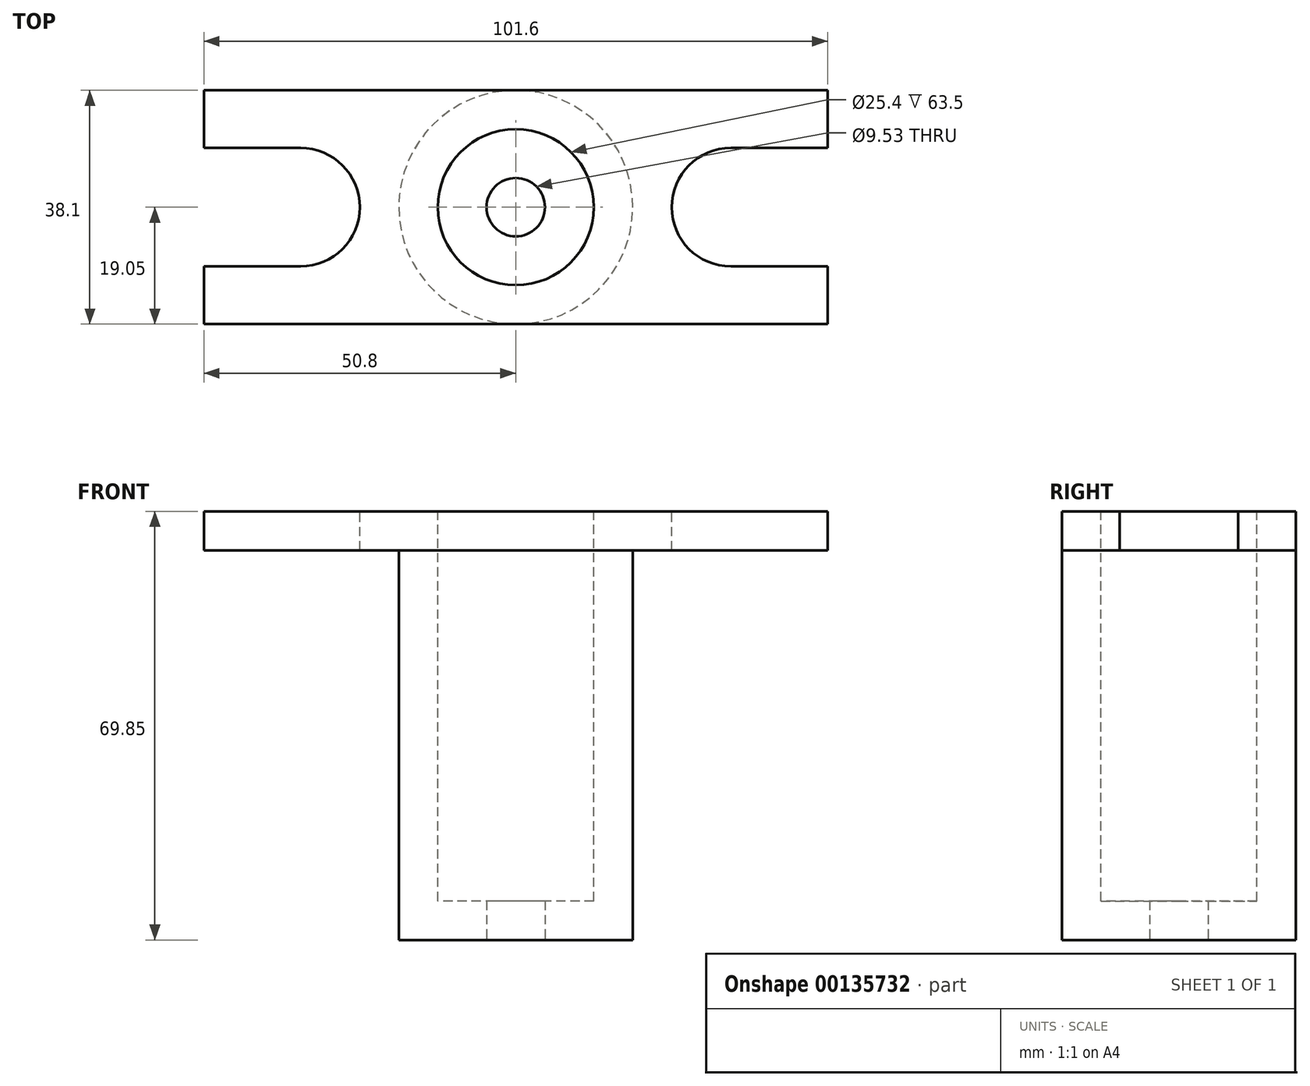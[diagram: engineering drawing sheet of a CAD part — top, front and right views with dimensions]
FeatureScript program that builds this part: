
annotation { "Feature Type Name" : "Feature", "Feature Type Description" : "" }
export const myFeature = defineFeature(function(context is Context, id is Id, definition is map)
    precondition{}
    {
        {
            var Q0;
            Q0=qCreatedBy(makeId("Top.planeOp"),FACE);
            var sketch = newSketch(context, id + "F0", { "sketchPlane" : qUnion([Q0])});
            skCircle(sketch, "E0", {"center": v(0, 0) * mm, "radius": 19.05 * mm});
            skSolve(sketch);
        }
        {
            var Q0;
            Q0 = qSketchRegion(id + "F0", true);
            extrude(context, id + "F1", {"entities" : qUnion([Q0]), "depth" : 69.85 * mm});
        }
        {
            var Q0;
            Q0=makeQuery(id+"F1.opExtrude","CAP_FACE",FACE,{"disambiguationData":[OSD([sQuery(id+"F0.wireOp",EDGE,"E0")])],"isStart":false});
            var sketch = newSketch(context, id + "F2", { "sketchPlane" : qUnion([Q0])});
            skCircle(sketch, "E1", {"center": v(0, 0) * mm, "radius": 12.7 * mm});
            skSolve(sketch);
        }
        {
            var Q0;
            Q0 = qSketchRegion(id + "F2", true);
            extrude(context, id + "F3", {"entities" : qUnion([Q0]), "operationType" : NewBodyOperationType.REMOVE, "oppositeDirection" : true, "depth" : 63.5 * mm});
        }
        {
            var Q0;
            Q0=makeQuery(id+"F1.opExtrude","CAP_FACE",FACE,{"disambiguationData":[OSD([sQuery(id+"F0.wireOp",EDGE,"E0")])],"isStart":false});
            var sketch = newSketch(context, id + "F4", { "sketchPlane" : qUnion([Q0])});
            skLineSegment(sketch, "E2.bottom", {"start": v(-50.8, 19.05) * mm, "end": v(50.8, 19.05) * mm});
            skLineSegment(sketch, "E2.top", {"start": v(-50.8, -19.05) * mm, "end": v(50.8, -19.05) * mm});
            skLineSegment(sketch, "E2.left", {"start": v(-50.8, 19.05) * mm, "end": v(-50.8, 9.65) * mm});
            skLineSegment(sketch, "E2.right", {"start": v(50.8, 19.05) * mm, "end": v(50.8, 9.65) * mm});
            skArc(sketch, "E3", {"start": v(35.05, 9.65) * mm, "mid": v(25.4, 0) * mm, "end": v(35.05, -9.65) * mm});
            skArc(sketch, "E4", {"start": v(-35.05, -9.65) * mm, "mid": v(-25.4, 0) * mm, "end": v(-35.05, 9.65) * mm});
            skLineSegment(sketch, "E5", {"start": v(35.05, -9.65) * mm, "end": v(50.8, -9.65) * mm});
            skLineSegment(sketch, "E6", {"start": v(35.05, 9.65) * mm, "end": v(50.8, 9.65) * mm});
            skLineSegment(sketch, "E7.trimOffspring", {"start": v(50.8, -9.65) * mm, "end": v(50.8, -19.05) * mm});
            skLineSegment(sketch, "E8", {"start": v(-35.05, 9.65) * mm, "end": v(-50.8, 9.65) * mm});
            skLineSegment(sketch, "E9", {"start": v(-35.05, -9.65) * mm, "end": v(-50.8, -9.65) * mm});
            skLineSegment(sketch, "E10.trimOffspring", {"start": v(-50.8, -9.65) * mm, "end": v(-50.8, -19.05) * mm});
            skSolve(sketch);
        }
        {
            var Q0;
            {var subQ4=sQuery(id+"F4.wireOp",EDGE,"E2.right");Q0=makeQuery(id+"F4.imprint","IMPRINT",FACE,{"disambiguationData":[TD([[makeQuery(id+"F4.imprint","IMPRINT",EDGE,{"derivedFrom":subQ4}),-1.0]])]});}
            var Q1;
            {var subQ0=sQuery(id+"F4.wireOp",EDGE,"E2.left");Q1=makeQuery(id+"F4.imprint","IMPRINT",FACE,{"disambiguationData":[TD([[makeQuery(id+"F4.imprint","IMPRINT",EDGE,{"derivedFrom":subQ0}),1.0]])]});}
            extrude(context, id + "F5", {"entities" : qUnion([Q0, Q1]), "operationType" : NewBodyOperationType.ADD, "oppositeDirection" : true, "depth" : 6.35 * mm});
        }
        {
            var Q0;
            Q0=makeQuery(id+"F1.opExtrude","CAP_FACE",FACE,{"disambiguationData":[OSD([sQuery(id+"F0.wireOp",EDGE,"E0")])],"isStart":true});
            var sketch = newSketch(context, id + "F6", { "sketchPlane" : qUnion([Q0])});
            skCircle(sketch, "E11", {"center": v(0, 0) * mm, "radius": 4.76 * mm});
            skSolve(sketch);
        }
        {
            var Q0;
            Q0 = qSketchRegion(id + "F6", true);
            extrude(context, id + "F7", {"entities" : qUnion([Q0]), "operationType" : NewBodyOperationType.REMOVE, "endBound" : BoundingType.THROUGH_ALL, "oppositeDirection" : true, "depth" : 25.4 * mm});
        }
    });
